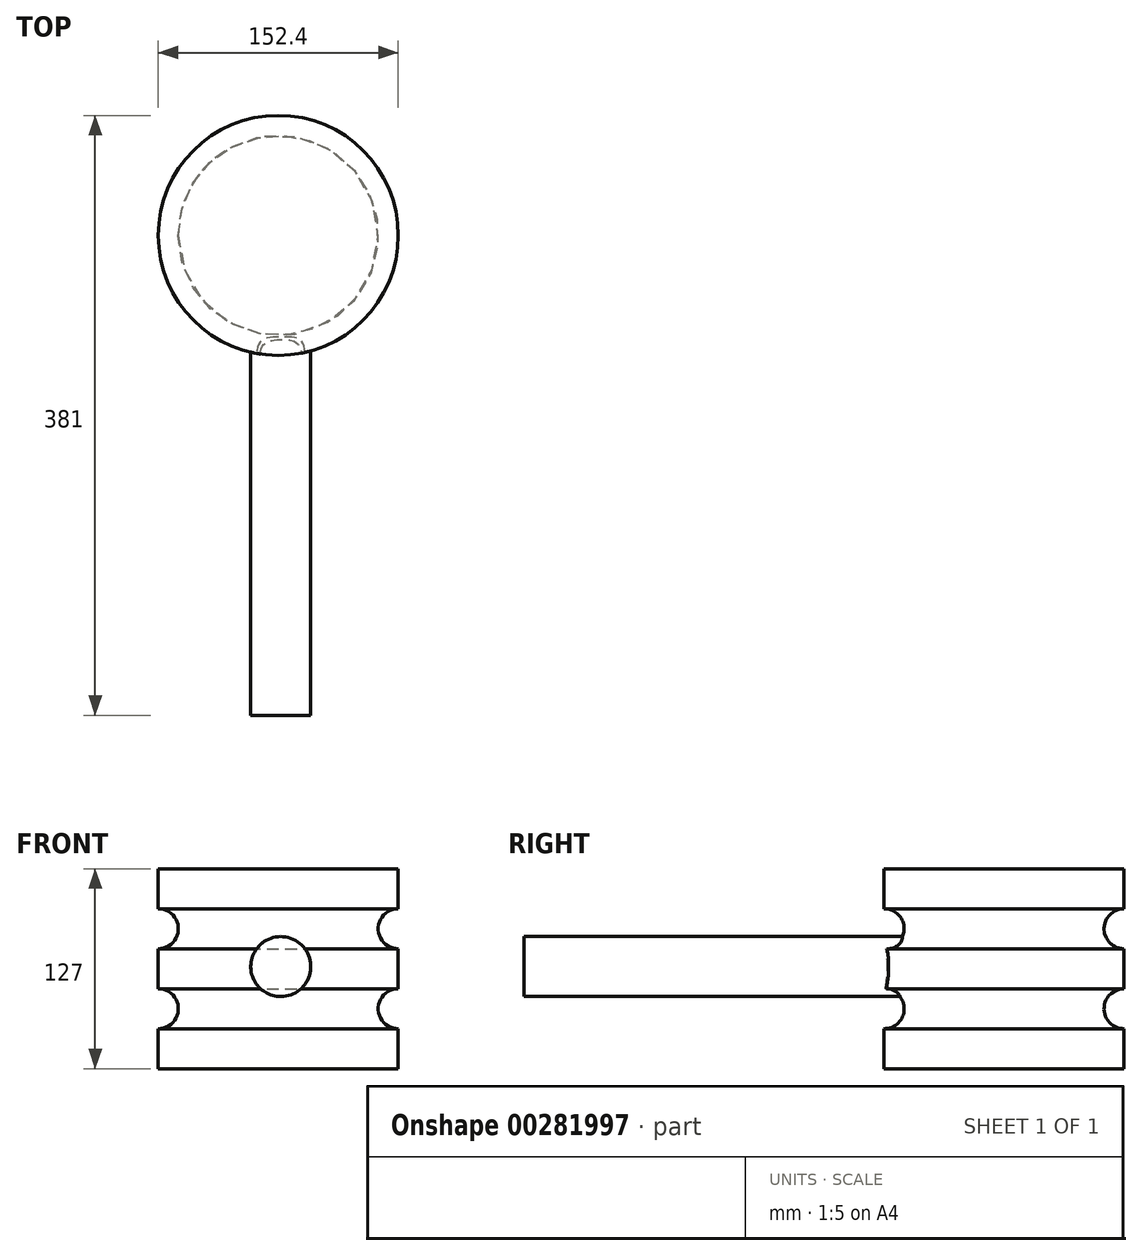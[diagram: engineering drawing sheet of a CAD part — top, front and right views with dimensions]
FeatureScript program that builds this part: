
annotation { "Feature Type Name" : "Feature", "Feature Type Description" : "" }
export const myFeature = defineFeature(function(context is Context, id is Id, definition is map)
    precondition{}
    {
        {
            var Q0;
            Q0=qCreatedBy(makeId("Front.planeOp"),FACE);
            var sketch = newSketch(context, id + "F0", { "sketchPlane" : qUnion([Q0])});
            skLineSegment(sketch, "E0.bottom", {"start": v(38, -0.76) * mm, "end": v(-38.2, -0.76) * mm});
            skLineSegment(sketch, "E0.top", {"start": v(38, 126.24) * mm, "end": v(-38.2, 126.24) * mm});
            skLineSegment(sketch, "E0.left", {"start": v(38, -0.76) * mm, "end": v(38, 24.64) * mm});
            skLineSegment(sketch, "E0.right", {"start": v(-38.2, -0.76) * mm, "end": v(-38.2, 126.24) * mm});
            skArc(sketch, "E1", {"start": v(38, 100.84) * mm, "mid": v(25.3, 88.14) * mm, "end": v(38, 75.44) * mm});
            skArc(sketch, "E2", {"start": v(38, 50.04) * mm, "mid": v(25.3, 37.34) * mm, "end": v(38, 24.64) * mm});
            skLineSegment(sketch, "E3.trimOffspring", {"start": v(38, 100.84) * mm, "end": v(38, 126.24) * mm});
            skLineSegment(sketch, "E4.trimOffspring", {"start": v(38, 50.04) * mm, "end": v(38, 75.44) * mm});
            skSolve(sketch);
        }
        {
            var Q0;
            Q0 = qSketchRegion(id + "F0", true);
            var Q1;
            Q1=sQuery(id+"F0.wireOp",EDGE,"E0.right");
            revolve(context, id + "F1", {"entities" : qUnion([Q0]), "axis" : qUnion([Q1]), "revolveType" : RevolveType.FULL});
        }
        {
            var Q0;
            Q0=qCreatedBy(makeId("Front.planeOp"),FACE);
            var sketch = newSketch(context, id + "F2", { "sketchPlane" : qUnion([Q0])});
            skCircle(sketch, "E5", {"center": v(-36.6, 64.08) * mm, "radius": 19.05 * mm});
            skSolve(sketch);
        }
        {
            var Q0;
            Q0 = qSketchRegion(id + "F2", true);
            extrude(context, id + "F3", {"entities" : qUnion([Q0]), "operationType" : NewBodyOperationType.ADD, "depth" : 304.8 * mm});
        }
    });
